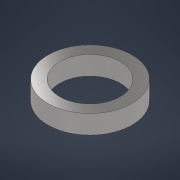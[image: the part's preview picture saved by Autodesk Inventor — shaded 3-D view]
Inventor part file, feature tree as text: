
AUTODESK INVENTOR PART (.ipt)
format: ipt  version: 2021 (Build 250183000, 183)  size: 95,744 bytes
history: native  units: mm
features: extrude x1, sketch x1
ambient origin geometry x8: Origin, YZ Plane, XZ Plane, XY Plane, X Axis, Y Axis, Z Axis, Center Point
bodies: Solid1 (feature_tree)
feature tree (2):
  extrude  "Extrusion1"  Depth=8.0mm
  sketch  "Sketch1"  dims[d0=26.0mm d1=36.0mm d2=8.0mm d3=0.0mm]
